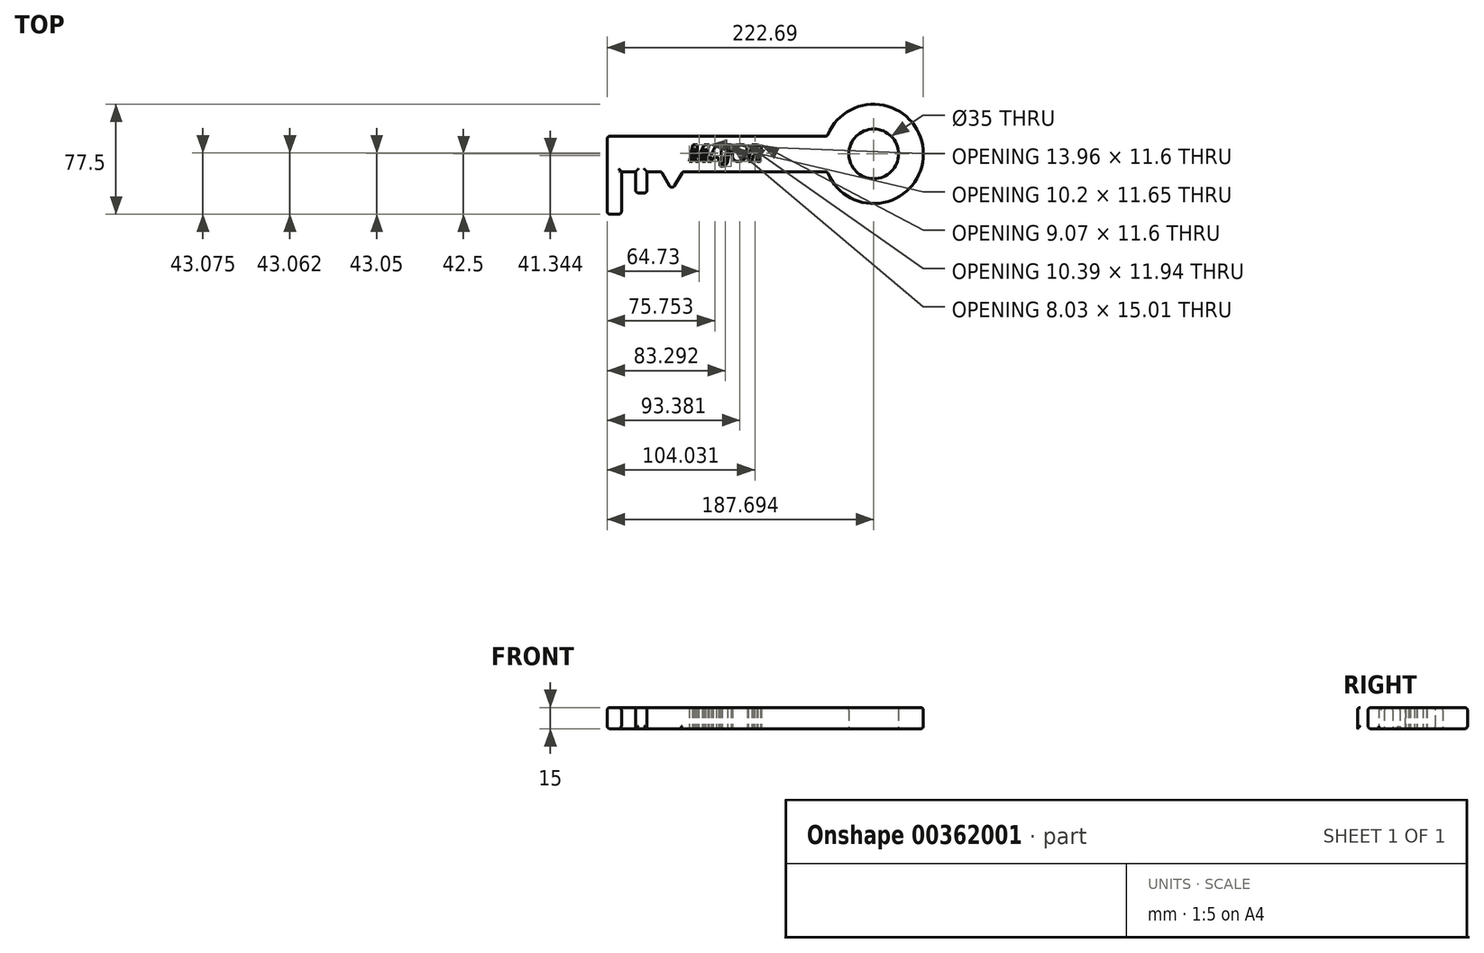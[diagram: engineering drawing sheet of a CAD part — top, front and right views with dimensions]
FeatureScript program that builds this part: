
annotation { "Feature Type Name" : "Feature", "Feature Type Description" : "" }
export const myFeature = defineFeature(function(context is Context, id is Id, definition is map)
    precondition{}
    {
        {
            var Q0;
            Q0=qCreatedBy(makeId("Top.planeOp"),FACE);
            var sketch = newSketch(context, id + "F0", { "sketchPlane" : qUnion([Q0])});
            skLineSegment(sketch, "E0.bottom", {"start": v(14.55, 12.5) * mm, "end": v(-140.45, 12.5) * mm});
            skLineSegment(sketch, "E0.top", {"start": v(14.55, -12.5) * mm, "end": v(-87.3, -12.5) * mm});
            skLineSegment(sketch, "E0.right", {"start": v(-140.45, 12.5) * mm, "end": v(-140.45, -12.5) * mm});
            skLineSegment(sketch, "E1.top", {"start": v(-140.45, -42.5) * mm, "end": v(-130.45, -42.5) * mm});
            skLineSegment(sketch, "E1.left", {"start": v(-140.45, -12.5) * mm, "end": v(-140.45, -42.5) * mm});
            skLineSegment(sketch, "E1.right", {"start": v(-130.45, -12.5) * mm, "end": v(-130.45, -42.5) * mm});
            skLineSegment(sketch, "E2.top", {"start": v(-120.45, -27.5) * mm, "end": v(-112.45, -27.5) * mm});
            skLineSegment(sketch, "E2.left", {"start": v(-120.45, -12.5) * mm, "end": v(-120.45, -27.5) * mm});
            skLineSegment(sketch, "E2.right", {"start": v(-112.45, -12.5) * mm, "end": v(-112.45, -27.5) * mm});
            skLineSegment(sketch, "E3", {"start": v(-102.45, -12.5) * mm, "end": v(-94.87, -25.45) * mm});
            skLineSegment(sketch, "E4", {"start": v(-94.87, -25.45) * mm, "end": v(-87.3, -12.5) * mm});
            skArc(sketch, "E5", {"start": v(14.55, -12.5) * mm, "mid": v(82.24, 0) * mm, "end": v(14.55, 12.5) * mm});
            skCircle(sketch, "E6", {"center": v(47.24, 0) * mm, "radius": 17.5 * mm});
            skLineSegment(sketch, "E7.trimOffspring", {"start": v(-102.45, -12.5) * mm, "end": v(-112.45, -12.5) * mm});
            skLineSegment(sketch, "E8.trimOffspring", {"start": v(-120.45, -12.5) * mm, "end": v(-130.45, -12.5) * mm});
            skLineSegment(sketch, "E9", {"start": v(47.24, 0) * mm, "end": v(-140.45, 0) * mm, "construction": true});
            skText(sketch, "E10", { "text": "MAJOR", "fontName": "OpenSans-BoldItalic.ttf"});
            const initialGuessF0  = {"E10": [-0.08312, -0.00525, 1, 0, 0.0117]};
            skSetInitialGuess(sketch, initialGuessF0);
            skSolve(sketch);
        }
        {
            var Q0;
            Q0=makeQuery(id+"F0.imprint","IMPRINT",FACE,{"disambiguationData":[TD([[makeQuery(id+"F0.imprint","IMPRINT",EDGE,{"derivedFrom":sQuery(id+"F0.wireOp",EDGE,"E0.bottom")}),1.0]])]});
            extrude(context, id + "F1", {"entities" : qUnion([Q0]), "depth" : 15 * mm});
        }
        {
            var Q0;
            Q0=makeQuery(id+"F1.opExtrude","CAP_EDGE",EDGE,{"disambiguationData":[OSD([sQuery(id+"F0.wireOp",EDGE,"E0.bottom")])],"isStart":false});
            var Q1;
            Q1=makeQuery(id+"F1.opExtrude","CAP_EDGE",EDGE,{"disambiguationData":[OSD([sQuery(id+"F0.wireOp",EDGE,"E5")])],"isStart":false});
            var Q2;
            Q2=makeQuery(id+"F1.opExtrude","CAP_EDGE",EDGE,{"disambiguationData":[OSD([sQuery(id+"F0.wireOp",EDGE,"E0.top")])],"isStart":false});
            var Q3;
            Q3=makeQuery(id+"F1.opExtrude","CAP_EDGE",EDGE,{"disambiguationData":[OSD([sQuery(id+"F0.wireOp",EDGE,"E6")])],"isStart":false});
            var Q4;
            Q4=makeQuery(id+"F1.opExtrude","CAP_EDGE",EDGE,{"disambiguationData":[OSD([sQuery(id+"F0.wireOp",EDGE,"E4")])],"isStart":false});
            var Q5;
            Q5=makeQuery(id+"F1.opExtrude","CAP_EDGE",EDGE,{"disambiguationData":[OSD([sQuery(id+"F0.wireOp",EDGE,"E3")])],"isStart":false});
            var Q6;
            Q6=makeQuery(id+"F1.opExtrude","CAP_EDGE",EDGE,{"disambiguationData":[OSD([sQuery(id+"F0.wireOp",EDGE,"E7.trimOffspring")])],"isStart":false});
            var Q7;
            Q7=makeQuery(id+"F1.opExtrude","CAP_EDGE",EDGE,{"disambiguationData":[OSD([sQuery(id+"F0.wireOp",EDGE,"E2.right")])],"isStart":false});
            var Q8;
            Q8=makeQuery(id+"F1.opExtrude","CAP_EDGE",EDGE,{"disambiguationData":[OSD([sQuery(id+"F0.wireOp",EDGE,"E2.left")])],"isStart":false});
            var Q9;
            Q9=makeQuery(id+"F1.opExtrude","CAP_EDGE",EDGE,{"disambiguationData":[OSD([sQuery(id+"F0.wireOp",EDGE,"E1.right")])],"isStart":false});
            var Q10;
            Q10=makeQuery(id+"F1.opExtrude","CAP_EDGE",EDGE,{"disambiguationData":[OSD([sQuery(id+"F0.wireOp",EDGE,"E0.right"),sQuery(id+"F0.wireOp",EDGE,"E1.left")])],"isStart":false});
            var Q11;
            Q11=makeQuery(id+"F1.opExtrude","CAP_EDGE",EDGE,{"disambiguationData":[OSD([sQuery(id+"F0.wireOp",EDGE,"E1.top")])],"isStart":false});
            var Q12;
            Q12=makeQuery(id+"F1.opExtrude","CAP_EDGE",EDGE,{"disambiguationData":[OSD([sQuery(id+"F0.wireOp",EDGE,"E0.bottom")])],"isStart":true});
            var Q13;
            Q13=makeQuery(id+"F1.opExtrude","SWEPT_EDGE",EDGE,{"disambiguationData":[OSD([sQuery(id+"F0.wireOp",EDGE,"E0.bottom"),sQuery(id+"F0.wireOp",EDGE,"E0.right")])]});
            var Q14;
            Q14=makeQuery(id+"F1.opExtrude","CAP_EDGE",EDGE,{"disambiguationData":[OSD([sQuery(id+"F0.wireOp",EDGE,"E0.right"),sQuery(id+"F0.wireOp",EDGE,"E1.left")])],"isStart":true});
            var Q15;
            Q15=makeQuery(id+"F1.opExtrude","SWEPT_EDGE",EDGE,{"disambiguationData":[OSD([sQuery(id+"F0.wireOp",EDGE,"E1.top"),sQuery(id+"F0.wireOp",EDGE,"E1.left")])]});
            var Q16;
            Q16=makeQuery(id+"F1.opExtrude","CAP_EDGE",EDGE,{"disambiguationData":[OSD([sQuery(id+"F0.wireOp",EDGE,"E5")])],"isStart":true});
            var Q17;
            Q17=makeQuery(id+"F1.opExtrude","CAP_EDGE",EDGE,{"disambiguationData":[OSD([sQuery(id+"F0.wireOp",EDGE,"E1.right")])],"isStart":true});
            var Q18;
            Q18=makeQuery(id+"F1.opExtrude","CAP_EDGE",EDGE,{"disambiguationData":[OSD([sQuery(id+"F0.wireOp",EDGE,"E2.top")])],"isStart":true});
            var Q19;
            Q19=makeQuery(id+"F1.opExtrude","SWEPT_EDGE",EDGE,{"disambiguationData":[OSD([sQuery(id+"F0.wireOp",EDGE,"E1.top"),sQuery(id+"F0.wireOp",EDGE,"E1.right")])]});
            var Q20;
            Q20=makeQuery(id+"F1.opExtrude","SWEPT_EDGE",EDGE,{"disambiguationData":[OSD([sQuery(id+"F0.wireOp",EDGE,"E2.top"),sQuery(id+"F0.wireOp",EDGE,"E2.left")])]});
            var Q21;
            Q21=makeQuery(id+"F1.opExtrude","SWEPT_EDGE",EDGE,{"disambiguationData":[OSD([sQuery(id+"F0.wireOp",EDGE,"E3"),sQuery(id+"F0.wireOp",EDGE,"E7.trimOffspring")])]});
            var Q22;
            Q22=makeQuery(id+"F1.opExtrude","SWEPT_EDGE",EDGE,{"disambiguationData":[OSD([sQuery(id+"F0.wireOp",EDGE,"E3"),sQuery(id+"F0.wireOp",EDGE,"E4")])]});
            var Q23;
            Q23=makeQuery(id+"F1.opExtrude","SWEPT_EDGE",EDGE,{"disambiguationData":[OSD([sQuery(id+"F0.wireOp",EDGE,"E0.top"),sQuery(id+"F0.wireOp",EDGE,"E4")])]});
            var Q24;
            Q24=makeQuery(id+"F1.opExtrude","SWEPT_EDGE",EDGE,{"disambiguationData":[OSD([sQuery(id+"F0.wireOp",EDGE,"E2.top"),sQuery(id+"F0.wireOp",EDGE,"E2.right")])]});
            var Q25;
            Q25=makeQuery(id+"F1.opExtrude","SWEPT_EDGE",EDGE,{"disambiguationData":[OSD([sQuery(id+"F0.wireOp",EDGE,"E0.bottom"),sQuery(id+"F0.wireOp",EDGE,"E5")])]});
            var Q26;
            Q26=makeQuery(id+"F1.opExtrude","SWEPT_FACE",FACE,{"disambiguationData":[OSD([sQuery(id+"F0.wireOp",EDGE,"E0.top")])]});
            var Q27;
            Q27=makeQuery(id+"F1.opExtrude","CAP_EDGE",EDGE,{"disambiguationData":[OSD([sQuery(id+"F0.wireOp",EDGE,"E8.trimOffspring")])],"isStart":false});
            fillet(context, id + "F2", {"entities" : qUnion([Q0, Q1, Q2, Q3, Q4, Q5, Q6, Q7, Q8, Q9, Q10, Q11, Q12, Q13, Q14, Q15, Q16, Q17, Q18, Q19, Q20, Q21, Q22, Q23, Q24, Q25, Q26, Q27]), "radius" : 2 * mm, "tangentPropagation" : true, "allowEdgeOverflow" : false});
        }
    });
